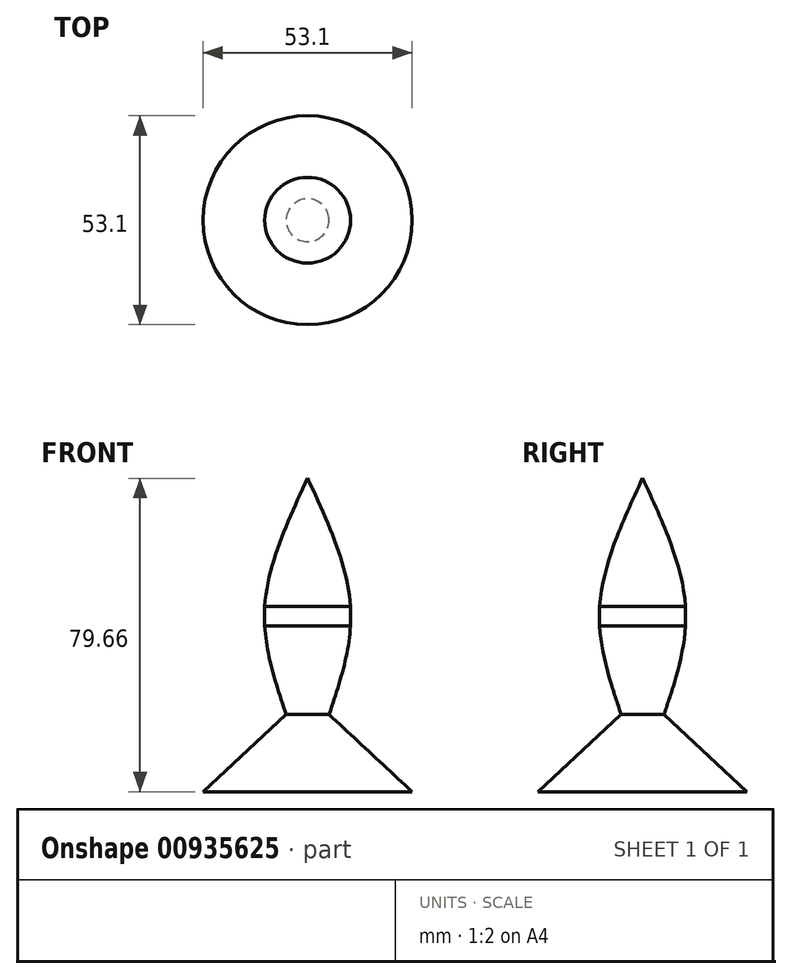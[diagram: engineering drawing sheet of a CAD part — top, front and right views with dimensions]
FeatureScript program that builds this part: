
annotation { "Feature Type Name" : "Feature", "Feature Type Description" : "" }
export const myFeature = defineFeature(function(context is Context, id is Id, definition is map)
    precondition{}
    {
        {
            var Q0;
            Q0=qCreatedBy(makeId("Front.planeOp"),FACE);
            var sketch = newSketch(context, id + "F0", { "sketchPlane" : qUnion([Q0])});
            skLineSegment(sketch, "E0", {"start": v(0, 0) * mm, "end": v(26.55, 0) * mm});
            skLineSegment(sketch, "E1", {"start": v(26.55, 0) * mm, "end": v(10.9, 14.56) * mm});
            skLineSegment(sketch, "E2", {"start": v(10.9, 42.14) * mm, "end": v(10.9, 47.11) * mm});
            skLineSegment(sketch, "E3", {"start": v(0, 79.66) * mm, "end": v(0, 24.7) * mm});
            skLineSegment(sketch, "E4", {"start": v(10.9, 14.56) * mm, "end": v(0, 24.7) * mm});
            skFitSpline(sketch, "E5", {"points": [v(5.45, 19.64) * mm, v(10.9, 47.11) * mm, v(0, 79.66) * mm], "startDerivative": vector(19.13, 56.93) * mm, "endDerivative": vector(-29.22, 63.02) * mm});
            skPoint(sketch, "E6.orphan", {"position": v(10.9, 79.66) * mm});
            skLineSegment(sketch, "E7", {"start": v(0, 24.7) * mm, "end": v(0, 0) * mm});
            skSolve(sketch);
        }
        {
            var Q0;
            {var subQ1=sQuery(id+"F0.wireOp",EDGE,"E2");Q0=makeQuery(id+"F0.imprint","IMPRINT",FACE,{"disambiguationData":[TD([[makeQuery(id+"F0.imprint","IMPRINT",EDGE,{"derivedFrom":subQ1}),1.0]])]});}
            var Q1;
            Q1=makeQuery(id+"F0.imprint","IMPRINT",FACE,{"disambiguationData":[TD([[makeQuery(id+"F0.imprint","IMPRINT",EDGE,{"derivedFrom":sQuery(id+"F0.wireOp",EDGE,"E0")}),1.0]])]});
            var Q2;
            Q2=sQuery(id+"F0.wireOp",EDGE,"E3");
            revolve(context, id + "F1", {"surfaceOperationType" : NewSurfaceOperationType.NEW, "entities" : qUnion([Q0, Q1]), "axis" : qUnion([Q2]), "revolveType" : RevolveType.FULL});
        }
    });
